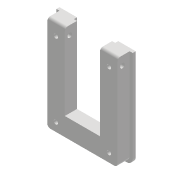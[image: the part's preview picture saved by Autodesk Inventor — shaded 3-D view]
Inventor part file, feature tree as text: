
AUTODESK INVENTOR PART (.ipt)
format: ipt  version: 2022 (Build 260153000, 153)  size: 174,592 bytes
history: native  units: mm
features: sketch x5, extrude x4, projected_geometry x3, fillet x1, hole x1
ambient origin geometry x8: Origin, YZ Plane, XZ Plane, XY Plane, X Axis, Y Axis, Z Axis, Center Point
bodies: Volumenkörper1 (feature_tree)
feature tree (14):
  extrude  "Extrusion1"  Depth=76.0mm
  extrude  "Extrusion2"  Depth=50.0mm
  extrude  "Extrusion3"  Depth=10.0mm
  fillet  "Rundung1"  Radius=10.0mm
  extrude  "Extrusion4"  Depth=25.0mm TaperAngle=0.0deg
  hole  "Bohrung1"  [1 undecoded]
  sketch  "Skizze1"  dims[d0=23.0mm d1=76.0mm]
  sketch  "Skizze2"  dims[d2=12.0mm d3=50.0mm]
  sketch  "Skizze3"  dims[d4=50.0mm d5=46.0mm d6=10.0mm d7=0.0mm]
  projected_geometry  "Projizierte Kontur1"
  sketch  "Skizze4"  dims[d8=0.5mm d9=25.0mm d10=0.0mm]
  projected_geometry  "Projizierte Kontur2"
  sketch  "Skizze5"  dims[d11=3.0mm d12=10.0mm d13=0.0mm d14=2.0mm d15=2.0mm d16=2.0mm d17=0.0mm d18=2.0mm d19=2.0mm d20=0.0mm d21=2.8mm d22=6.0mm d23=4.0mm d24=2.0mm d25=90.0deg d26=12.0mm d27=20.594885mm]
  projected_geometry  "Projizierte Kontur3"
note: 1 required parameter value undecoded (feature->parameter linkage not recoverable at this tier; creation-order binding heuristic only, values carry confidence <= 0.55)
